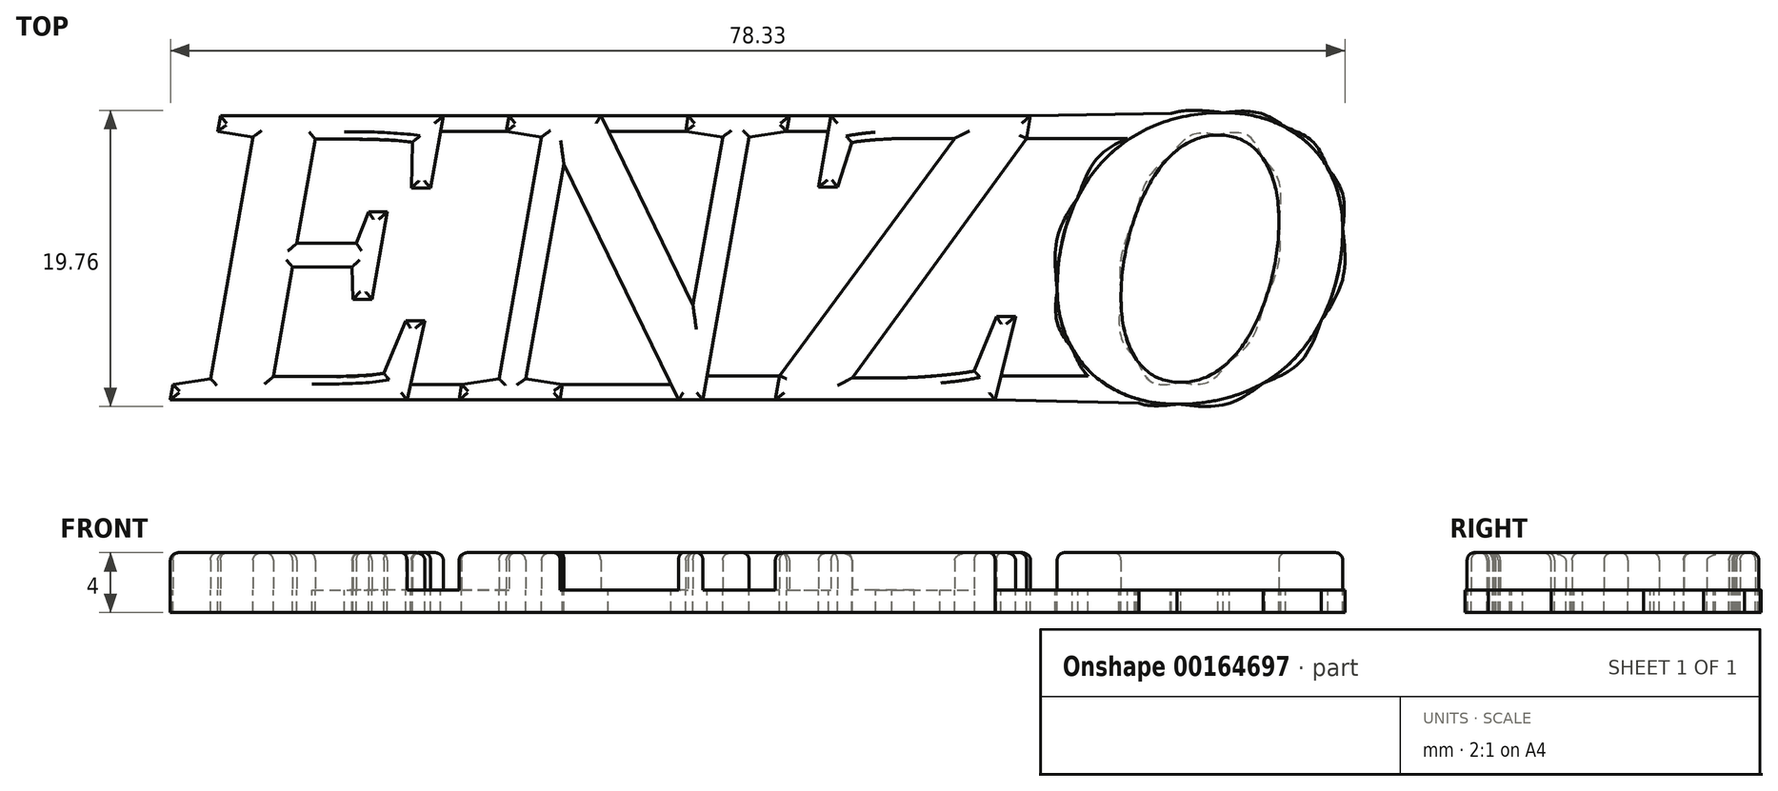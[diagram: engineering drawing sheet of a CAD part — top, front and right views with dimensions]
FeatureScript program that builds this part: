
annotation { "Feature Type Name" : "Feature", "Feature Type Description" : "" }
export const myFeature = defineFeature(function(context is Context, id is Id, definition is map)
    precondition{}
    {
        {
            var Q0;
            Q0=qCreatedBy(makeId("Top.planeOp"),FACE);
            var sketch = newSketch(context, id + "F0", { "sketchPlane" : qUnion([Q0])});
            skText(sketch, "E0", { "text": "ENZO", "fontName": "Tinos-BoldItalic.ttf"});
            const initialGuessF0  = {"E0": [0, 0, 1, 0, 0.02084]};
            skSetInitialGuess(sketch, initialGuessF0);
            skSolve(sketch);
        }
        {
            var Q0;
            Q0=makeQuery(id+"F0.imprint","IMPRINT",FACE,{"disambiguationData":[TD([[makeQuery(id+"F0.imprint","IMPRINT",EDGE,{"derivedFrom":sQuery(id+"F0.wireOp",EDGE,"E0.sketch_text.stroke-0")}),-1.0]])]});
            var Q1;
            Q1=makeQuery(id+"F0.imprint","IMPRINT",FACE,{"disambiguationData":[TD([[makeQuery(id+"F0.imprint","IMPRINT",EDGE,{"derivedFrom":sQuery(id+"F0.wireOp",EDGE,"E0.sketch_text.stroke-26")}),-1.0]])]});
            var Q2;
            Q2=makeQuery(id+"F0.imprint","IMPRINT",FACE,{"disambiguationData":[TD([[makeQuery(id+"F0.imprint","IMPRINT",EDGE,{"derivedFrom":sQuery(id+"F0.wireOp",EDGE,"E0.sketch_text.stroke-46")}),-1.0]])]});
            var Q3;
            Q3=makeQuery(id+"F0.imprint","IMPRINT",FACE,{"disambiguationData":[TD([[makeQuery(id+"F0.imprint","IMPRINT",EDGE,{"derivedFrom":sQuery(id+"F0.wireOp",EDGE,"E0.sketch_text.stroke-64")}),-1.0]])]});
            extrude(context, id + "F1", {"entities" : qUnion([Q0, Q1, Q2, Q3]), "depth" : 2.5 * mm});
        }
        {
            var Q0;
            Q0=qCreatedBy(makeId("Top.planeOp"),FACE);
            var sketch = newSketch(context, id + "F2", { "sketchPlane" : qUnion([Q0])});
            skLineSegment(sketch, "E1.0.0", {"start": v(2.46, 1.42) * mm, "end": v(5.3, 17.55) * mm});
            skLineSegment(sketch, "E1.0.1", {"start": v(5.3, 17.55) * mm, "end": v(2.94, 17.92) * mm});
            skLineSegment(sketch, "E1.0.2", {"start": v(2.94, 17.92) * mm, "end": v(3.13, 18.96) * mm});
            skLineSegment(sketch, "E1.0.3", {"start": v(3.13, 18.96) * mm, "end": v(18, 18.96) * mm});
            skLineSegment(sketch, "E1.0.4", {"start": v(17.81, 17.92) * mm, "end": v(17.15, 14.13) * mm});
            skLineSegment(sketch, "E1.0.5", {"start": v(17.15, 14.13) * mm, "end": v(15.86, 14.13) * mm});
            skLineSegment(sketch, "E1.0.6", {"start": v(15.86, 14.13) * mm, "end": v(15.94, 17.2) * mm});
            skFitSpline(sketch, "E1.0.7", {"points": [v(15.94, 17.2) * mm, v(14.4, 17.4) * mm, v(11.4, 17.4) * mm]});
            skLineSegment(sketch, "E1.0.8", {"start": v(11.4, 17.4) * mm, "end": v(9.46, 17.4) * mm});
            skLineSegment(sketch, "E1.0.9", {"start": v(9.46, 17.4) * mm, "end": v(8.23, 10.44) * mm});
            skLineSegment(sketch, "E1.0.10", {"start": v(8.23, 10.44) * mm, "end": v(12.2, 10.44) * mm});
            skLineSegment(sketch, "E1.0.11", {"start": v(12.2, 10.44) * mm, "end": v(13, 12.54) * mm});
            skLineSegment(sketch, "E1.0.12", {"start": v(13, 12.54) * mm, "end": v(14.26, 12.54) * mm});
            skLineSegment(sketch, "E1.0.13", {"start": v(14.26, 12.54) * mm, "end": v(13.23, 6.71) * mm});
            skLineSegment(sketch, "E1.0.14", {"start": v(13.23, 6.71) * mm, "end": v(11.97, 6.71) * mm});
            skLineSegment(sketch, "E1.0.15", {"start": v(11.97, 6.71) * mm, "end": v(11.91, 8.86) * mm});
            skLineSegment(sketch, "E1.0.16", {"start": v(11.91, 8.86) * mm, "end": v(7.94, 8.86) * mm});
            skLineSegment(sketch, "E1.0.17", {"start": v(7.94, 8.86) * mm, "end": v(6.66, 1.56) * mm});
            skLineSegment(sketch, "E1.0.18", {"start": v(6.66, 1.56) * mm, "end": v(9.24, 1.56) * mm});
            skFitSpline(sketch, "E1.0.19", {"points": [v(9.24, 1.56) * mm, v(12.82, 1.56) * mm, v(14.02, 1.78) * mm]});
            skLineSegment(sketch, "E1.0.20", {"start": v(14.02, 1.78) * mm, "end": v(15.48, 5.29) * mm});
            skLineSegment(sketch, "E1.0.21", {"start": v(15.48, 5.29) * mm, "end": v(16.76, 5.29) * mm});
            skLineSegment(sketch, "E1.0.22", {"start": v(16.76, 5.29) * mm, "end": v(15.8, 1.03) * mm});
            skLineSegment(sketch, "E1.0.23", {"start": v(15.58, 0) * mm, "end": v(-0.21, 0) * mm});
            skLineSegment(sketch, "E1.0.24", {"start": v(-0.21, 0) * mm, "end": v(-0.04, 1.03) * mm});
            skLineSegment(sketch, "E1.0.25", {"start": v(-0.04, 1.03) * mm, "end": v(2.46, 1.42) * mm});
            skLineSegment(sketch, "E1.1.0", {"start": v(34.64, 6.32) * mm, "end": v(36.62, 17.55) * mm});
            skLineSegment(sketch, "E1.1.1", {"start": v(36.62, 17.55) * mm, "end": v(34.15, 17.92) * mm});
            skLineSegment(sketch, "E1.1.3", {"start": v(34.33, 18.96) * mm, "end": v(41.08, 18.96) * mm});
            skLineSegment(sketch, "E1.1.5", {"start": v(40.9, 17.92) * mm, "end": v(38.39, 17.55) * mm});
            skLineSegment(sketch, "E1.1.6", {"start": v(38.39, 17.55) * mm, "end": v(35.6, 1.61) * mm});
            skLineSegment(sketch, "E1.1.7", {"start": v(35.3, 0) * mm, "end": v(33.68, 0) * mm});
            skLineSegment(sketch, "E1.1.8", {"start": v(33.18, 1.03) * mm, "end": v(26.04, 15.72) * mm});
            skLineSegment(sketch, "E1.1.9", {"start": v(26.04, 15.72) * mm, "end": v(23.48, 1.42) * mm});
            skLineSegment(sketch, "E1.1.10", {"start": v(23.48, 1.42) * mm, "end": v(25.95, 1.03) * mm});
            skLineSegment(sketch, "E1.1.12", {"start": v(25.78, 0) * mm, "end": v(19.04, 0) * mm});
            skLineSegment(sketch, "E1.1.14", {"start": v(19.2, 1.03) * mm, "end": v(21.7, 1.42) * mm});
            skLineSegment(sketch, "E1.1.15", {"start": v(21.7, 1.42) * mm, "end": v(24.55, 17.55) * mm});
            skLineSegment(sketch, "E1.1.16", {"start": v(24.55, 17.55) * mm, "end": v(22.2, 17.92) * mm});
            skLineSegment(sketch, "E1.1.18", {"start": v(22.37, 18.96) * mm, "end": v(28.5, 18.96) * mm});
            skLineSegment(sketch, "E1.1.19", {"start": v(29, 17.92) * mm, "end": v(34.64, 6.32) * mm});
            skLineSegment(sketch, "E1.2.0", {"start": v(40.43, 1.61) * mm, "end": v(52.1, 17.45) * mm});
            skLineSegment(sketch, "E1.2.1", {"start": v(52.1, 17.45) * mm, "end": v(49.38, 17.45) * mm});
            skFitSpline(sketch, "E1.2.2", {"points": [v(49.38, 17.45) * mm, v(47.99, 17.45) * mm, v(46.84, 17.36) * mm]});
            skFitSpline(sketch, "E1.2.3", {"points": [v(46.84, 17.36) * mm, v(45.7, 17.27) * mm, v(45.25, 17.17) * mm]});
            skLineSegment(sketch, "E1.2.4", {"start": v(45.25, 17.17) * mm, "end": v(44.28, 14.2) * mm});
            skLineSegment(sketch, "E1.2.5", {"start": v(44.28, 14.2) * mm, "end": v(43.03, 14.2) * mm});
            skLineSegment(sketch, "E1.2.6", {"start": v(43.03, 14.2) * mm, "end": v(43.68, 17.92) * mm});
            skLineSegment(sketch, "E1.2.7", {"start": v(43.86, 18.96) * mm, "end": v(57.16, 18.96) * mm});
            skLineSegment(sketch, "E1.2.9", {"start": v(56.9, 17.45) * mm, "end": v(45.26, 1.47) * mm});
            skLineSegment(sketch, "E1.2.10", {"start": v(45.26, 1.47) * mm, "end": v(47.9, 1.47) * mm});
            skFitSpline(sketch, "E1.2.11", {"points": [v(47.9, 1.47) * mm, v(49.44, 1.47) * mm, v(51.12, 1.63) * mm]});
            skFitSpline(sketch, "E1.2.12", {"points": [v(51.12, 1.63) * mm, v(52.8, 1.8) * mm, v(53.41, 1.94) * mm]});
            skLineSegment(sketch, "E1.2.13", {"start": v(53.41, 1.94) * mm, "end": v(54.88, 5.55) * mm});
            skLineSegment(sketch, "E1.2.14", {"start": v(54.88, 5.55) * mm, "end": v(56.16, 5.55) * mm});
            skLineSegment(sketch, "E1.2.15", {"start": v(56.16, 5.55) * mm, "end": v(55.2, 1.61) * mm});
            skLineSegment(sketch, "E1.2.16", {"start": v(54.8, 0) * mm, "end": v(40.14, 0) * mm});
            skFitSpline(sketch, "E1.3.0", {"points": [v(72.67, 1.12) * mm, v(70.2, -0.28) * mm, v(66.92, -0.28) * mm]});
            skFitSpline(sketch, "E1.3.1", {"points": [v(66.92, -0.28) * mm, v(64.58, -0.28) * mm, v(62.76, 0.69) * mm]});
            skFitSpline(sketch, "E1.3.2", {"points": [v(62.76, 0.69) * mm, v(60.95, 1.66) * mm, v(59.94, 3.41) * mm]});
            skFitSpline(sketch, "E1.3.3", {"points": [v(59.94, 3.41) * mm, v(58.94, 5.17) * mm, v(58.94, 7.4) * mm]});
            skFitSpline(sketch, "E1.3.4", {"points": [v(58.94, 7.4) * mm, v(58.94, 10.83) * mm, v(60.32, 13.53) * mm]});
            skFitSpline(sketch, "E1.3.5", {"points": [v(60.32, 13.53) * mm, v(61.7, 16.24) * mm, v(64.22, 17.7) * mm]});
            skFitSpline(sketch, "E1.3.6", {"points": [v(64.22, 17.7) * mm, v(66.73, 19.17) * mm, v(70, 19.17) * mm]});
            skFitSpline(sketch, "E1.3.7", {"points": [v(70, 19.17) * mm, v(72.34, 19.17) * mm, v(74.15, 18.2) * mm]});
            skFitSpline(sketch, "E1.3.8", {"points": [v(74.15, 18.2) * mm, v(75.97, 17.23) * mm, v(76.97, 15.47) * mm]});
            skFitSpline(sketch, "E1.3.9", {"points": [v(76.97, 15.47) * mm, v(77.98, 13.7) * mm, v(77.98, 11.48) * mm]});
            skFitSpline(sketch, "E1.3.10", {"points": [v(77.98, 11.48) * mm, v(77.98, 8.09) * mm, v(76.56, 5.3) * mm]});
            skFitSpline(sketch, "E1.3.11", {"points": [v(76.56, 5.3) * mm, v(75.14, 2.53) * mm, v(72.67, 1.12) * mm]});
            skLineSegment(sketch, "E2", {"start": v(15.58, 0) * mm, "end": v(19.04, 0) * mm});
            skLineSegment(sketch, "E3", {"start": v(19.2, 1.03) * mm, "end": v(15.8, 1.03) * mm});
            skLineSegment(sketch, "E4", {"start": v(25.78, 0) * mm, "end": v(33.68, 0) * mm});
            skLineSegment(sketch, "E5", {"start": v(25.95, 1.03) * mm, "end": v(33.18, 1.03) * mm});
            skLineSegment(sketch, "E6", {"start": v(35.3, 0) * mm, "end": v(40.14, 0) * mm});
            skLineSegment(sketch, "E7", {"start": v(40.43, 1.61) * mm, "end": v(35.6, 1.61) * mm});
            skLineSegment(sketch, "E8", {"start": v(54.8, 0) * mm, "end": v(66.92, -0.28) * mm});
            skLineSegment(sketch, "E9", {"start": v(55.2, 1.61) * mm, "end": v(61.41, 1.61) * mm});
            skLineSegment(sketch, "E10", {"start": v(18, 18.96) * mm, "end": v(22.37, 18.96) * mm});
            skLineSegment(sketch, "E11", {"start": v(41.08, 18.96) * mm, "end": v(43.86, 18.96) * mm});
            skLineSegment(sketch, "E12", {"start": v(34.33, 18.96) * mm, "end": v(28.5, 18.96) * mm});
            skLineSegment(sketch, "E13", {"start": v(34.15, 17.92) * mm, "end": v(29, 17.92) * mm});
            skLineSegment(sketch, "E14", {"start": v(22.2, 17.92) * mm, "end": v(17.81, 17.92) * mm});
            skLineSegment(sketch, "E15", {"start": v(40.9, 17.92) * mm, "end": v(43.68, 17.92) * mm});
            skLineSegment(sketch, "E16", {"start": v(57.16, 18.96) * mm, "end": v(70, 19.17) * mm});
            skLineSegment(sketch, "E17", {"start": v(56.9, 17.45) * mm, "end": v(63.8, 17.45) * mm});
            skPoint(sketch, "E18.orphan", {"position": v(62.76, 0.69) * mm});
            skPoint(sketch, "E19.orphan", {"position": v(64.22, 17.7) * mm});
            skFitSpline(sketch, "E20.0", {"points": [v(63.2, 6.86) * mm, v(63.2, 4.2) * mm, v(64.24, 2.68) * mm]});
            skFitSpline(sketch, "E21.0", {"points": [v(64.24, 2.68) * mm, v(65.28, 1.17) * mm, v(67.18, 1.17) * mm]});
            skFitSpline(sketch, "E22.0", {"points": [v(67.18, 1.17) * mm, v(68.95, 1.17) * mm, v(70.4, 2.57) * mm]});
            skFitSpline(sketch, "E23.0", {"points": [v(70.4, 2.57) * mm, v(71.86, 3.97) * mm, v(72.8, 6.6) * mm]});
            skFitSpline(sketch, "E24.0", {"points": [v(72.8, 6.6) * mm, v(73.72, 9.23) * mm, v(73.72, 11.91) * mm]});
            skFitSpline(sketch, "E25.0", {"points": [v(73.72, 11.91) * mm, v(73.72, 14.6) * mm, v(72.65, 16.14) * mm]});
            skFitSpline(sketch, "E26.0", {"points": [v(72.65, 16.14) * mm, v(71.57, 17.68) * mm, v(69.65, 17.68) * mm]});
            skFitSpline(sketch, "E27.0", {"points": [v(69.65, 17.68) * mm, v(67.93, 17.68) * mm, v(66.48, 16.27) * mm]});
            skFitSpline(sketch, "E28.0", {"points": [v(66.48, 16.27) * mm, v(65.03, 14.85) * mm, v(64.11, 12.18) * mm]});
            skFitSpline(sketch, "E29.0", {"points": [v(64.11, 12.18) * mm, v(63.2, 9.5) * mm, v(63.2, 6.86) * mm]});
            skSolve(sketch);
        }
        {
            var Q0;
            Q0 = qSketchRegion(id + "F2", true);
            extrude(context, id + "F3", {"entities" : qUnion([Q0]), "operationType" : NewBodyOperationType.ADD, "oppositeDirection" : true, "depth" : 1.5 * mm});
        }
        {
            var Q0;
            Q0=makeQuery(id+"F1.opExtrude","CAP_FACE",FACE,{"disambiguationData":[OSD([sQuery(id+"F0.wireOp",EDGE,"E0.sketch_text.stroke-64"),sQuery(id+"F0.wireOp",EDGE,"E0.sketch_text.stroke-65"),sQuery(id+"F0.wireOp",EDGE,"E0.sketch_text.stroke-66"),sQuery(id+"F0.wireOp",EDGE,"E0.sketch_text.stroke-67"),sQuery(id+"F0.wireOp",EDGE,"E0.sketch_text.stroke-68"),sQuery(id+"F0.wireOp",EDGE,"E0.sketch_text.stroke-69"),sQuery(id+"F0.wireOp",EDGE,"E0.sketch_text.stroke-70"),sQuery(id+"F0.wireOp",EDGE,"E0.sketch_text.stroke-71"),sQuery(id+"F0.wireOp",EDGE,"E0.sketch_text.stroke-72"),sQuery(id+"F0.wireOp",EDGE,"E0.sketch_text.stroke-73"),sQuery(id+"F0.wireOp",EDGE,"E0.sketch_text.stroke-74"),sQuery(id+"F0.wireOp",EDGE,"E0.sketch_text.stroke-75"),sQuery(id+"F0.wireOp",EDGE,"E0.sketch_text.stroke-76"),sQuery(id+"F0.wireOp",EDGE,"E0.sketch_text.stroke-77"),sQuery(id+"F0.wireOp",EDGE,"E0.sketch_text.stroke-78"),sQuery(id+"F0.wireOp",EDGE,"E0.sketch_text.stroke-79"),sQuery(id+"F0.wireOp",EDGE,"E0.sketch_text.stroke-80"),sQuery(id+"F0.wireOp",EDGE,"E0.sketch_text.stroke-81"),sQuery(id+"F0.wireOp",EDGE,"E0.sketch_text.stroke-82"),sQuery(id+"F0.wireOp",EDGE,"E0.sketch_text.stroke-83"),sQuery(id+"F0.wireOp",EDGE,"E0.sketch_text.stroke-84"),sQuery(id+"F0.wireOp",EDGE,"E0.sketch_text.stroke-85")])],"isStart":false});
            var Q1;
            Q1=makeQuery(id+"F1.opExtrude","CAP_FACE",FACE,{"disambiguationData":[OSD([sQuery(id+"F0.wireOp",EDGE,"E0.sketch_text.stroke-46"),sQuery(id+"F0.wireOp",EDGE,"E0.sketch_text.stroke-47"),sQuery(id+"F0.wireOp",EDGE,"E0.sketch_text.stroke-48"),sQuery(id+"F0.wireOp",EDGE,"E0.sketch_text.stroke-49"),sQuery(id+"F0.wireOp",EDGE,"E0.sketch_text.stroke-50"),sQuery(id+"F0.wireOp",EDGE,"E0.sketch_text.stroke-51"),sQuery(id+"F0.wireOp",EDGE,"E0.sketch_text.stroke-52"),sQuery(id+"F0.wireOp",EDGE,"E0.sketch_text.stroke-53"),sQuery(id+"F0.wireOp",EDGE,"E0.sketch_text.stroke-54"),sQuery(id+"F0.wireOp",EDGE,"E0.sketch_text.stroke-55"),sQuery(id+"F0.wireOp",EDGE,"E0.sketch_text.stroke-56"),sQuery(id+"F0.wireOp",EDGE,"E0.sketch_text.stroke-57"),sQuery(id+"F0.wireOp",EDGE,"E0.sketch_text.stroke-58"),sQuery(id+"F0.wireOp",EDGE,"E0.sketch_text.stroke-59"),sQuery(id+"F0.wireOp",EDGE,"E0.sketch_text.stroke-60"),sQuery(id+"F0.wireOp",EDGE,"E0.sketch_text.stroke-61"),sQuery(id+"F0.wireOp",EDGE,"E0.sketch_text.stroke-62"),sQuery(id+"F0.wireOp",EDGE,"E0.sketch_text.stroke-63")])],"isStart":false});
            var Q2;
            Q2=makeQuery(id+"F1.opExtrude","CAP_FACE",FACE,{"disambiguationData":[OSD([sQuery(id+"F0.wireOp",EDGE,"E0.sketch_text.stroke-26"),sQuery(id+"F0.wireOp",EDGE,"E0.sketch_text.stroke-27"),sQuery(id+"F0.wireOp",EDGE,"E0.sketch_text.stroke-28"),sQuery(id+"F0.wireOp",EDGE,"E0.sketch_text.stroke-29"),sQuery(id+"F0.wireOp",EDGE,"E0.sketch_text.stroke-30"),sQuery(id+"F0.wireOp",EDGE,"E0.sketch_text.stroke-31"),sQuery(id+"F0.wireOp",EDGE,"E0.sketch_text.stroke-32"),sQuery(id+"F0.wireOp",EDGE,"E0.sketch_text.stroke-33"),sQuery(id+"F0.wireOp",EDGE,"E0.sketch_text.stroke-34"),sQuery(id+"F0.wireOp",EDGE,"E0.sketch_text.stroke-35"),sQuery(id+"F0.wireOp",EDGE,"E0.sketch_text.stroke-36"),sQuery(id+"F0.wireOp",EDGE,"E0.sketch_text.stroke-37"),sQuery(id+"F0.wireOp",EDGE,"E0.sketch_text.stroke-38"),sQuery(id+"F0.wireOp",EDGE,"E0.sketch_text.stroke-39"),sQuery(id+"F0.wireOp",EDGE,"E0.sketch_text.stroke-40"),sQuery(id+"F0.wireOp",EDGE,"E0.sketch_text.stroke-41"),sQuery(id+"F0.wireOp",EDGE,"E0.sketch_text.stroke-42"),sQuery(id+"F0.wireOp",EDGE,"E0.sketch_text.stroke-43"),sQuery(id+"F0.wireOp",EDGE,"E0.sketch_text.stroke-44"),sQuery(id+"F0.wireOp",EDGE,"E0.sketch_text.stroke-45")])],"isStart":false});
            var Q3;
            Q3=makeQuery(id+"F1.opExtrude","CAP_FACE",FACE,{"disambiguationData":[OSD([sQuery(id+"F0.wireOp",EDGE,"E0.sketch_text.stroke-0"),sQuery(id+"F0.wireOp",EDGE,"E0.sketch_text.stroke-1"),sQuery(id+"F0.wireOp",EDGE,"E0.sketch_text.stroke-2"),sQuery(id+"F0.wireOp",EDGE,"E0.sketch_text.stroke-3"),sQuery(id+"F0.wireOp",EDGE,"E0.sketch_text.stroke-4"),sQuery(id+"F0.wireOp",EDGE,"E0.sketch_text.stroke-5"),sQuery(id+"F0.wireOp",EDGE,"E0.sketch_text.stroke-6"),sQuery(id+"F0.wireOp",EDGE,"E0.sketch_text.stroke-7"),sQuery(id+"F0.wireOp",EDGE,"E0.sketch_text.stroke-8"),sQuery(id+"F0.wireOp",EDGE,"E0.sketch_text.stroke-9"),sQuery(id+"F0.wireOp",EDGE,"E0.sketch_text.stroke-10"),sQuery(id+"F0.wireOp",EDGE,"E0.sketch_text.stroke-11"),sQuery(id+"F0.wireOp",EDGE,"E0.sketch_text.stroke-12"),sQuery(id+"F0.wireOp",EDGE,"E0.sketch_text.stroke-13"),sQuery(id+"F0.wireOp",EDGE,"E0.sketch_text.stroke-14"),sQuery(id+"F0.wireOp",EDGE,"E0.sketch_text.stroke-15"),sQuery(id+"F0.wireOp",EDGE,"E0.sketch_text.stroke-16"),sQuery(id+"F0.wireOp",EDGE,"E0.sketch_text.stroke-17"),sQuery(id+"F0.wireOp",EDGE,"E0.sketch_text.stroke-18"),sQuery(id+"F0.wireOp",EDGE,"E0.sketch_text.stroke-19"),sQuery(id+"F0.wireOp",EDGE,"E0.sketch_text.stroke-20"),sQuery(id+"F0.wireOp",EDGE,"E0.sketch_text.stroke-21"),sQuery(id+"F0.wireOp",EDGE,"E0.sketch_text.stroke-22"),sQuery(id+"F0.wireOp",EDGE,"E0.sketch_text.stroke-23"),sQuery(id+"F0.wireOp",EDGE,"E0.sketch_text.stroke-24"),sQuery(id+"F0.wireOp",EDGE,"E0.sketch_text.stroke-25")])],"isStart":false});
            fillet(context, id + "F4", {"entities" : qUnion([Q0, Q1, Q2, Q3]), "radius" : 0.5 * mm, "tangentPropagation" : true, "allowEdgeOverflow" : false});
        }
    });
